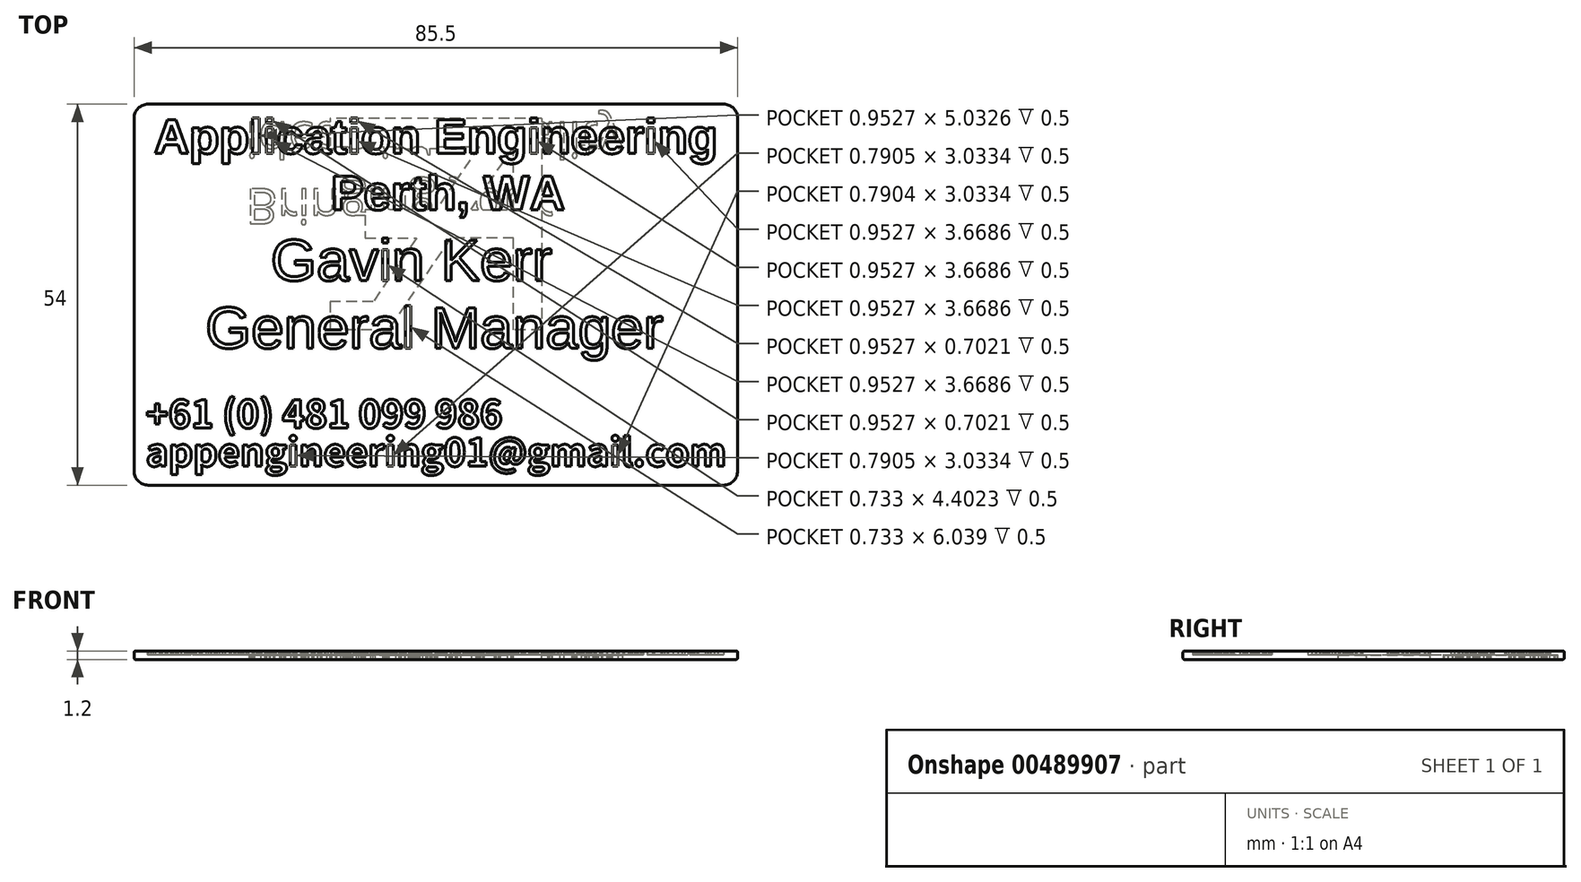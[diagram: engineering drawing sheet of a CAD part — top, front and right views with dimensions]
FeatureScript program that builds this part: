
annotation { "Feature Type Name" : "Feature", "Feature Type Description" : "" }
export const myFeature = defineFeature(function(context is Context, id is Id, definition is map)
    precondition{}
    {
        {
            var Q0;
            Q0=qCreatedBy(makeId("Top.planeOp"),FACE);
            var sketch = newSketch(context, id + "F0", { "sketchPlane" : qUnion([Q0])});
            skLineSegment(sketch, "E0.bottom", {"start": v(40.75, 27) * mm, "end": v(-40.75, 27) * mm});
            skLineSegment(sketch, "E0.top", {"start": v(40.75, -27) * mm, "end": v(-40.75, -27) * mm});
            skLineSegment(sketch, "E0.left", {"start": v(42.75, 25) * mm, "end": v(42.75, -25) * mm});
            skLineSegment(sketch, "E0.right", {"start": v(-42.75, 25) * mm, "end": v(-42.75, -25) * mm});
            skPoint(sketch, "E0.middle", {"position": v(0, 0) * mm});
            skPoint(sketch, "E1.visualSharp", {"position": v(-42.75, 27) * mm});
            skArc(sketch, "E1.filletArc", {"start": v(-40.75, 27) * mm, "mid": v(-42.16, 26.41) * mm, "end": v(-42.75, 25) * mm});
            skPoint(sketch, "E2.visualSharp", {"position": v(42.75, 27) * mm});
            skArc(sketch, "E2.filletArc", {"start": v(42.75, 25) * mm, "mid": v(42.16, 26.41) * mm, "end": v(40.75, 27) * mm});
            skPoint(sketch, "E3.visualSharp", {"position": v(42.75, -27) * mm});
            skArc(sketch, "E3.filletArc", {"start": v(40.75, -27) * mm, "mid": v(42.16, -26.41) * mm, "end": v(42.75, -25) * mm});
            skPoint(sketch, "E4.visualSharp", {"position": v(-42.75, -27) * mm});
            skArc(sketch, "E4.filletArc", {"start": v(-42.75, -25) * mm, "mid": v(-42.16, -26.41) * mm, "end": v(-40.75, -27) * mm});
            skSolve(sketch);
        }
        {
            var Q0;
            Q0=qSketchRegion(id+"F0",true);
            extrude(context, id + "F1", {"entities" : qUnion([Q0]), "endBound" : BoundingType.SYMMETRIC, "depth" : 1.2 * mm});
        }
        {
            var Q0;
            Q0=makeQuery(id+"F1.opExtrude","CAP_EDGE",EDGE,{"disambiguationData":[OSD([sQuery(id+"F0.wireOp",EDGE,"E0.bottom")])],"isStart":false});
            var Q1;
            Q1=makeQuery(id+"F1.opExtrude","CAP_EDGE",EDGE,{"disambiguationData":[OSD([sQuery(id+"F0.wireOp",EDGE,"E0.bottom")])],"isStart":true});
            fillet(context, id + "F2", {"entities" : qUnion([Q0, Q1]), "radius" : .2 * mm, "tangentPropagation" : true, "allowEdgeOverflow" : false});
        }
        {
            var Q0;
            Q0=qCreatedBy(makeId("Top.planeOp"),FACE);
            cPlane(context, id + "F3", {"entities" : qUnion([Q0]), "cplaneType" : CPlaneType.OFFSET, "offset" : .1 * mm, "width" : 150 * mm, "height" : 150 * mm});
        }
        {
            var Q0;
            Q0=qCreatedBy(id+"F3.planeOp",FACE);
            var sketch = newSketch(context, id + "F4", { "sketchPlane" : qUnion([Q0])});
            skText(sketch, "E5", { "text": "Application Engineering\n             Perth, WA", "fontName": "Arimo-Bold.ttf"});
            const initialGuessF4  = {"E5": [-0.03994, 0.02, 1, 0, 0.005]};
            skSetInitialGuess(sketch, initialGuessF4);
            skSolve(sketch);
        }
        {
            var Q0;
            Q0=qCreatedBy(id+"F3.planeOp",FACE);
            var sketch = newSketch(context, id + "F5", { "sketchPlane" : qUnion([Q0])});
            skText(sketch, "E6", { "text": "    Gavin Kerr\nGeneral Manager", "fontName": "Arimo-Regular.ttf"});
            const initialGuessF5  = {"E6": [-0.03264, 0.002, 1, 0, 0.006]};
            skSetInitialGuess(sketch, initialGuessF5);
            skSolve(sketch);
        }
        {
            var Q0;
            Q0=qCreatedBy(id+"F3.planeOp",FACE);
            var sketch = newSketch(context, id + "F6", { "sketchPlane" : qUnion([Q0])});
            skText(sketch, "E7", { "text": "+61 (0) 481 099 986\<email>", "fontName": "NotoSansCJKsc-Bold.otf"});
            const initialGuessF6  = {"E7": [-0.04107, -0.0189, 1, 0, 0.0039]};
            skSetInitialGuess(sketch, initialGuessF6);
            skSolve(sketch);
        }
        {
            var Q0;
            Q0=qSketchRegion(id+"F4",true);
            var Q1;
            Q1=qSketchRegion(id+"F5",true);
            var Q2;
            Q2=qSketchRegion(id+"F6",true);
            extrude(context, id + "F7", {"entities" : qUnion([Q0, Q1, Q2]), "operationType" : NewBodyOperationType.REMOVE, "depth" : .8 * mm});
        }
        {
            var Q0;
            Q0=qCreatedBy(makeId("Top.planeOp"),FACE);
            var sketch = newSketch(context, id + "F8", { "sketchPlane" : qUnion([Q0])});
            skLineSegment(sketch, "E8", {"start": v(0, -50.5) * mm, "end": v(0, 55.1) * mm, "construction": true});
            skSolve(sketch);
        }
        {
            var Q0;
            Q0=sQuery(id+"F8.wireOp",EDGE,"E8");
            cPlane(context, id + "F9", {"entities" : qUnion([Q0]), "cplaneType" : CPlaneType.LINE_ANGLE, "offset" : 25 * mm, "angle" : 180 * degree, "width" : 150 * mm, "height" : 150 * mm});
        }
        {
            var Q0;
            Q0=qCreatedBy(id+"F9.planeOp",FACE);
            var sketch = newSketch(context, id + "F10", { "sketchPlane" : qUnion([Q0])});
            skLineSegment(sketch, "E9", {"start": v(15, -25) * mm, "end": v(15, 5) * mm});
            skLineSegment(sketch, "E10", {"start": v(15, 5) * mm, "end": v(11, 5) * mm});
            skLineSegment(sketch, "E11", {"start": v(11, 5) * mm, "end": v(11, -8) * mm});
            skLineSegment(sketch, "E12", {"start": v(11, -8) * mm, "end": v(2.11, -8) * mm});
            skLineSegment(sketch, "E13", {"start": v(2.11, -8) * mm, "end": v(-6.78, 5) * mm});
            skLineSegment(sketch, "E14", {"start": v(-6.78, 5) * mm, "end": v(-15, 5) * mm});
            skLineSegment(sketch, "E15", {"start": v(15, -25) * mm, "end": v(-15, -25) * mm});
            skLineSegment(sketch, "E16", {"start": v(-15, -25) * mm, "end": v(-15, -21) * mm});
            skLineSegment(sketch, "E17", {"start": v(-15, -21) * mm, "end": v(6.15, -21) * mm});
            skLineSegment(sketch, "E18", {"start": v(6.15, -21) * mm, "end": v(0, -12) * mm});
            skLineSegment(sketch, "E19", {"start": v(0, -12) * mm, "end": v(-10, -12) * mm});
            skLineSegment(sketch, "E20", {"start": v(-10, -12) * mm, "end": v(-10, -8) * mm});
            skLineSegment(sketch, "E21", {"start": v(-10, -8) * mm, "end": v(-2.74, -8) * mm});
            skLineSegment(sketch, "E22", {"start": v(-2.74, -8) * mm, "end": v(-8.89, 1) * mm});
            skLineSegment(sketch, "E23", {"start": v(-8.89, 1) * mm, "end": v(-15, 1) * mm});
            skLineSegment(sketch, "E24", {"start": v(11, -12) * mm, "end": v(11, -21) * mm});
            skLineSegment(sketch, "E25", {"start": v(11, -21) * mm, "end": v(4.85, -12) * mm});
            skLineSegment(sketch, "E26", {"start": v(4.85, -12) * mm, "end": v(11, -12) * mm});
            skLineSegment(sketch, "E27", {"start": v(-15, 1) * mm, "end": v(-15, 5) * mm});
            skPoint(sketch, "E28.middle", {"position": v(0, -10) * mm});
            skSolve(sketch);
        }
        {
            var Q0;
            Q0=qCreatedBy(id+"F9.planeOp",FACE);
            var sketch = newSketch(context, id + "F11", { "sketchPlane" : qUnion([Q0])});
            skText(sketch, "E29", { "text": "Bringing your\nideas into reality", "fontName": "OpenSans-Regular.ttf"});
            const initialGuessF11  = {"E29": [-0.02693, -0.015, 1, 0, 0.005]};
            skSetInitialGuess(sketch, initialGuessF11);
            skSolve(sketch);
        }
        {
            var Q0;
            Q0=qSketchRegion(id+"F10",true);
            var Q1;
            Q1=qSketchRegion(id+"F11",true);
            extrude(context, id + "F12", {"entities" : qUnion([Q0, Q1]), "operationType" : NewBodyOperationType.REMOVE, "depth" : .8 * mm});
        }
    });
